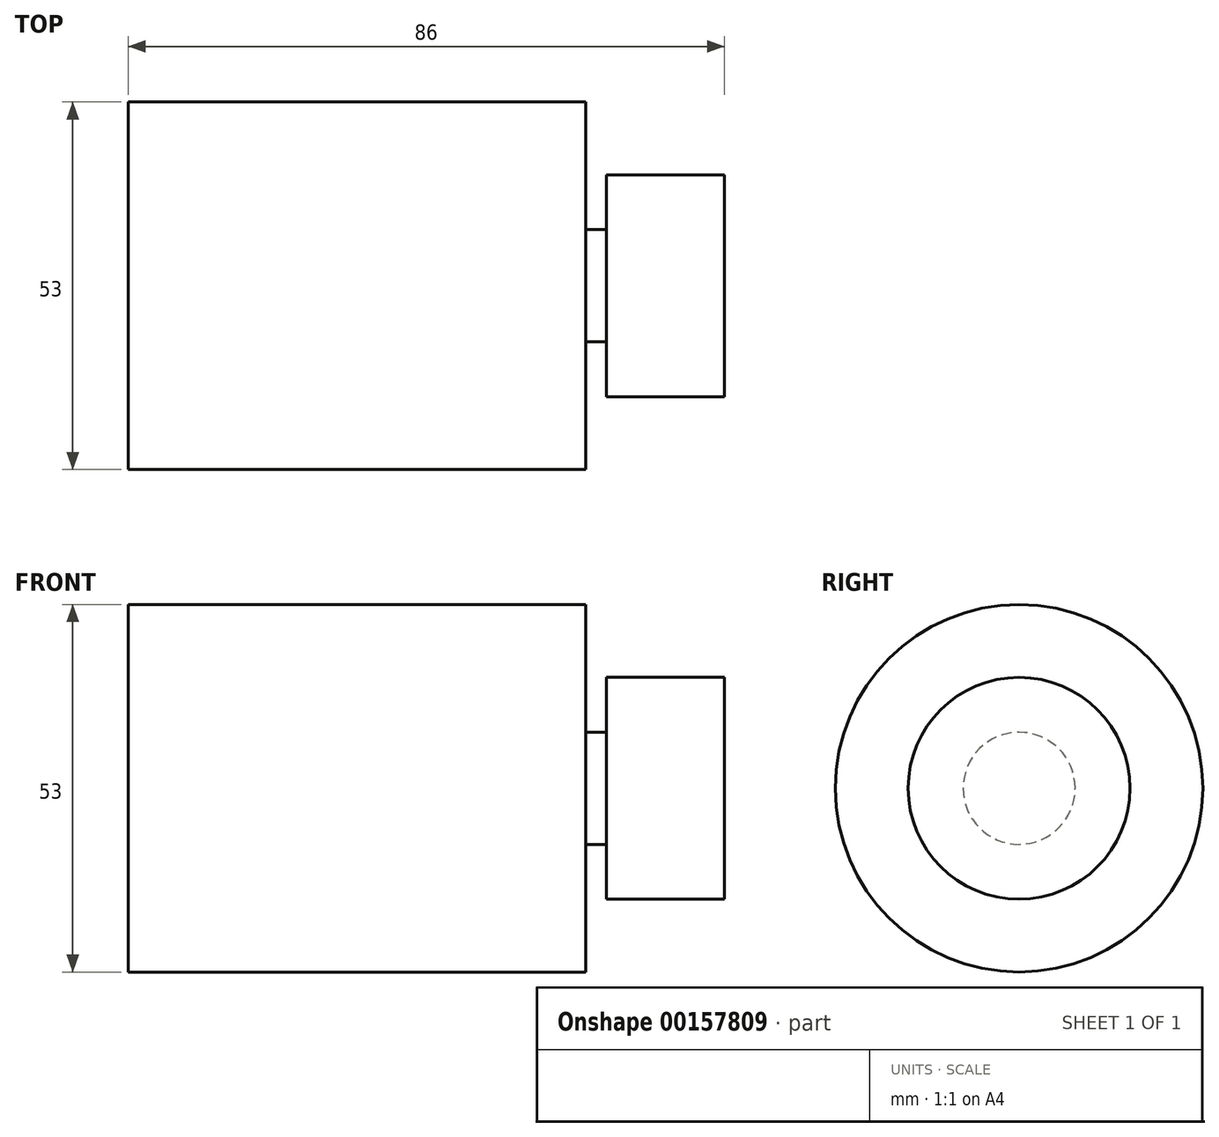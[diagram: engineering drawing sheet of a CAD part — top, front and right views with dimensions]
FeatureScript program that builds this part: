
annotation { "Feature Type Name" : "Feature", "Feature Type Description" : "" }
export const myFeature = defineFeature(function(context is Context, id is Id, definition is map)
    precondition{}
    {
        {
            var Q0;
            Q0=qCreatedBy(makeId("Top.planeOp"),FACE);
            var sketch = newSketch(context, id + "F0", { "sketchPlane" : qUnion([Q0])});
            skLineSegment(sketch, "E0", {"start": v(-42.13, 0) * mm, "end": v(-42.13, 26.5) * mm});
            skLineSegment(sketch, "E1", {"start": v(-42.13, 26.5) * mm, "end": v(23.87, 26.5) * mm});
            skLineSegment(sketch, "E2", {"start": v(23.87, 26.5) * mm, "end": v(23.87, 8.08) * mm});
            skLineSegment(sketch, "E3", {"start": v(23.87, 8.08) * mm, "end": v(26.87, 8.08) * mm});
            skLineSegment(sketch, "E4", {"start": v(26.87, 8.08) * mm, "end": v(26.87, 16) * mm});
            skLineSegment(sketch, "E5", {"start": v(26.87, 16) * mm, "end": v(43.87, 16) * mm});
            skLineSegment(sketch, "E6", {"start": v(43.87, 16) * mm, "end": v(43.87, 0) * mm});
            skLineSegment(sketch, "E7", {"start": v(43.87, 0) * mm, "end": v(-42.13, 0) * mm});
            skSolve(sketch);
        }
        {
            var Q0;
            Q0=makeQuery(id+"F0.imprint","IMPRINT",FACE,{"disambiguationData":[TD([[makeQuery(id+"F0.imprint","IMPRINT",EDGE,{"derivedFrom":sQuery(id+"F0.wireOp",EDGE,"E0")}),-1.0]])]});
            var Q1;
            Q1=sQuery(id+"F0.wireOp",EDGE,"E7");
            revolve(context, id + "F1", {"entities" : qUnion([Q0]), "axis" : qUnion([Q1]), "revolveType" : RevolveType.FULL});
        }
    });
